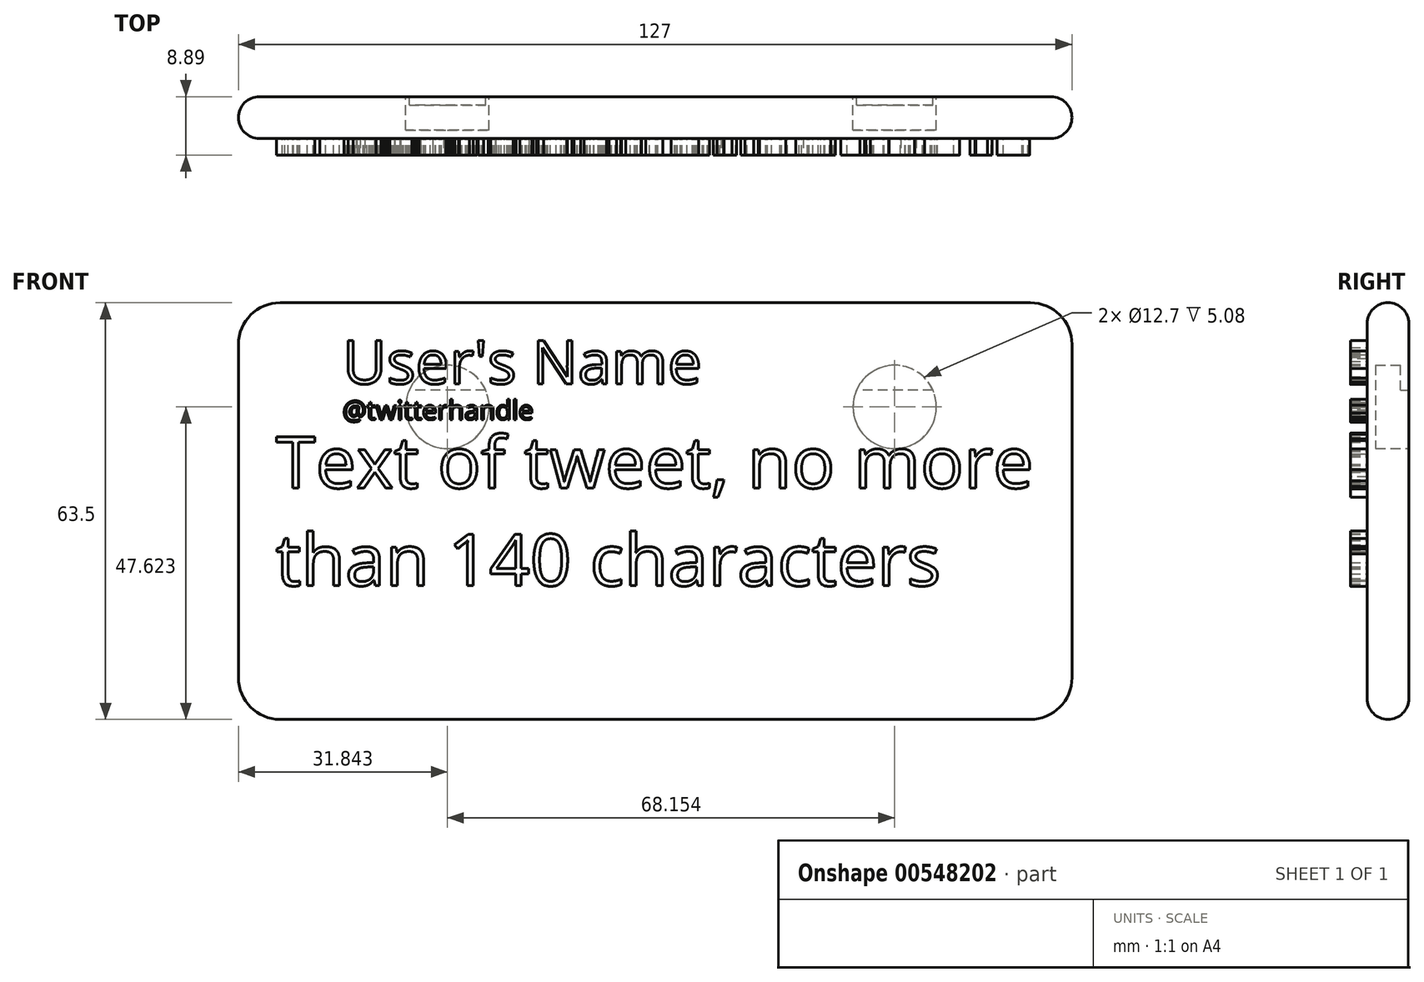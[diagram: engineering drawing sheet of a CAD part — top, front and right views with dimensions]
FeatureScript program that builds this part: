
annotation { "Feature Type Name" : "Feature", "Feature Type Description" : "" }
export const myFeature = defineFeature(function(context is Context, id is Id, definition is map)
    precondition{}
    {
        {
            var Q0;
            Q0=qCreatedBy(makeId("Front.planeOp"),FACE);
            var sketch = newSketch(context, id + "F0", { "sketchPlane" : qUnion([Q0])});
            skLineSegment(sketch, "E0.bottom", {"start": v(-127, 63.5) * mm, "end": v(0, 63.5) * mm});
            skLineSegment(sketch, "E0.top", {"start": v(-127, 0) * mm, "end": v(0, 0) * mm});
            skLineSegment(sketch, "E0.left", {"start": v(-127, 63.5) * mm, "end": v(-127, 0) * mm});
            skLineSegment(sketch, "E0.right", {"start": v(0, 63.5) * mm, "end": v(0, 0) * mm});
            skSolve(sketch);
        }
        {
            var Q0;
            Q0 = qSketchRegion(id + "F0", true);
            extrude(context, id + "F1", {"entities" : qUnion([Q0]), "depth" : 6.35 * mm, "offsetDistance" : 25.4 * mm});
        }
        {
            var Q0;
            Q0=makeQuery(id+"F1.opExtrude","SWEPT_EDGE",EDGE,{"disambiguationData":[OSD([sQuery(id+"F0.wireOp",EDGE,"E0.bottom"),sQuery(id+"F0.wireOp",EDGE,"E0.left")])]});
            var Q1;
            Q1=makeQuery(id+"F1.opExtrude","SWEPT_EDGE",EDGE,{"disambiguationData":[OSD([sQuery(id+"F0.wireOp",EDGE,"E0.bottom"),sQuery(id+"F0.wireOp",EDGE,"E0.right")])]});
            var Q2;
            Q2=makeQuery(id+"F1.opExtrude","SWEPT_EDGE",EDGE,{"disambiguationData":[OSD([sQuery(id+"F0.wireOp",EDGE,"E0.top"),sQuery(id+"F0.wireOp",EDGE,"E0.left")])]});
            var Q3;
            Q3=makeQuery(id+"F1.opExtrude","SWEPT_EDGE",EDGE,{"disambiguationData":[OSD([sQuery(id+"F0.wireOp",EDGE,"E0.top"),sQuery(id+"F0.wireOp",EDGE,"E0.right")])]});
            fillet(context, id + "F2", {"entities" : qUnion([Q0, Q1, Q2, Q3]), "radius" : 6.35 * mm, "tangentPropagation" : true, "allowEdgeOverflow" : false});
        }
        {
            var Q0;
            Q0=makeQuery(id+"F1.opExtrude","CAP_EDGE",EDGE,{"disambiguationData":[OSD([sQuery(id+"F0.wireOp",EDGE,"E0.bottom")])],"isStart":false});
            var Q1;
            Q1=makeQuery(id+"F1.opExtrude","CAP_EDGE",EDGE,{"disambiguationData":[OSD([sQuery(id+"F0.wireOp",EDGE,"E0.bottom")])],"isStart":true});
            fillet(context, id + "F3", {"entities" : qUnion([Q0, Q1]), "radius" : 3.17 * mm, "tangentPropagation" : true, "allowEdgeOverflow" : false});
        }
        {
            var Q0;
            Q0=makeQuery(id+"F1.opExtrude","CAP_FACE",FACE,{"disambiguationData":[OSD([sQuery(id+"F0.wireOp",EDGE,"E0.bottom"),sQuery(id+"F0.wireOp",EDGE,"E0.top"),sQuery(id+"F0.wireOp",EDGE,"E0.left"),sQuery(id+"F0.wireOp",EDGE,"E0.right")])],"isStart":true});
            var sketch = newSketch(context, id + "F4", { "sketchPlane" : qUnion([Q0])});
            skCircle(sketch, "E1", {"center": v(27, 47.62) * mm, "radius": 6.35 * mm});
            skCircle(sketch, "E2", {"center": v(95.16, 47.62) * mm, "radius": 6.35 * mm});
            skLineSegment(sketch, "E3", {"start": v(3.17, 47.62) * mm, "end": v(123.83, 47.62) * mm});
            skSolve(sketch);
        }
        {
            var Q0;
            Q0 = qSketchRegion(id + "F4", true);
            extrude(context, id + "F5", {"entities" : qUnion([Q0]), "operationType" : NewBodyOperationType.REMOVE, "oppositeDirection" : true, "depth" : 5.08 * mm, "offsetDistance" : 25.4 * mm});
        }
        {
            var Q0;
            Q0=makeQuery(id+"F1.opExtrude","CAP_FACE",FACE,{"disambiguationData":[OSD([sQuery(id+"F0.wireOp",EDGE,"E0.bottom"),sQuery(id+"F0.wireOp",EDGE,"E0.top"),sQuery(id+"F0.wireOp",EDGE,"E0.left"),sQuery(id+"F0.wireOp",EDGE,"E0.right")])],"isStart":true});
            var sketch = newSketch(context, id + "F6", { "sketchPlane" : qUnion([Q0])});
            skLineSegment(sketch, "E4", {"start": v(3.17, 50.16) * mm, "end": v(123.83, 50.16) * mm});
            skArc(sketch, "E5", {"start": v(32.82, 50.16) * mm, "mid": v(27, 53.97) * mm, "end": v(21.18, 50.16) * mm});
            skArc(sketch, "E6", {"start": v(100.98, 50.16) * mm, "mid": v(95.16, 53.97) * mm, "end": v(89.34, 50.16) * mm});
            skSolve(sketch);
        }
        {
            var Q0;
            Q0 = qSketchRegion(id + "F6", true);
            var Q1;
            Q1=makeQuery(id+"F5.opExtrude","CAP_FACE",FACE,{"disambiguationData":[OSD([sQuery(id+"F4.wireOp",EDGE,"E2")])],"isStart":false});
            extrude(context, id + "F7", {"entities" : qUnion([Q0, Q1]), "operationType" : NewBodyOperationType.ADD, "oppositeDirection" : true, "depth" : 1.27 * mm, "offsetDistance" : 25.4 * mm});
        }
        {
            var Q0;
            Q0=makeQuery(id+"F1.opExtrude","CAP_FACE",FACE,{"disambiguationData":[OSD([sQuery(id+"F0.wireOp",EDGE,"E0.bottom"),sQuery(id+"F0.wireOp",EDGE,"E0.top"),sQuery(id+"F0.wireOp",EDGE,"E0.left"),sQuery(id+"F0.wireOp",EDGE,"E0.right")])],"isStart":false});
            var sketch = newSketch(context, id + "F8", { "sketchPlane" : qUnion([Q0])});
            skText(sketch, "E7", { "text": "User\'s Name", "fontName": "OpenSans-Regular.ttf"});
            skText(sketch, "E8", { "text": "@twitterhandle", "fontName": "OpenSans-Regular.ttf"});
            skText(sketch, "E9", { "text": "Text of tweet, no more\nthan 140 characters", "fontName": "OpenSans-Regular.ttf"});
            const initialGuessF8  = {"E7": [-0.11113, 0.05114, 1, 0, 0.00664], "E8": [-0.11113, 0.04568, 1, 0, 0.00292], "E9": [-0.12129, 0.03526, 1, 0, 0.00788]};
            skSetInitialGuess(sketch, initialGuessF8);
            skSolve(sketch);
        }
        {
            var Q0;
            Q0 = qSketchRegion(id + "F8", true);
            extrude(context, id + "F9", {"entities" : qUnion([Q0]), "operationType" : NewBodyOperationType.ADD, "depth" : 2.54 * mm, "offsetDistance" : 25.4 * mm});
        }
    });
